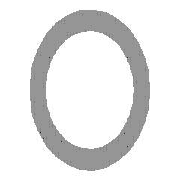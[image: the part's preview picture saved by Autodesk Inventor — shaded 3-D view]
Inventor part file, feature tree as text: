
AUTODESK INVENTOR PART (.ipt)
format: ipt  version: 2021 (Build 250183000, 183)  size: 231,424 bytes
history: native  units: mm (DEFAULTED — no unit token found)
features: other x5, plane x2, sketch x2, sweep x1
ambient origin geometry x8: Origin, YZ Plane, XZ Plane, XY Plane, X Axis, Y Axis, Z Axis, Center Point
bodies: Solid1 (feature_tree)
feature tree (10):
  parser-record x1  (decoder bookkeeping rows leaked as tree rows — omitted from the tree; the rows remain in map.json)
  other  "Driven Length"
  other  "Plano inicial"
  other  "Plano final"
  other  "Trayectoria de barrido"
  plane  "Plano de trabajo de orientación"
  sweep  "Cuerpo"
  sketch  "Sketch3"  dims[d0=33.528mm d1=4.5466mm]
  plane  "Work Plane3"
  sketch  "Sketch4"  dims[d4=-0.0mm d5=734.209592mm d6=90.0deg d7=734.209592mm d8=0.0mm d9=0.0mm]
